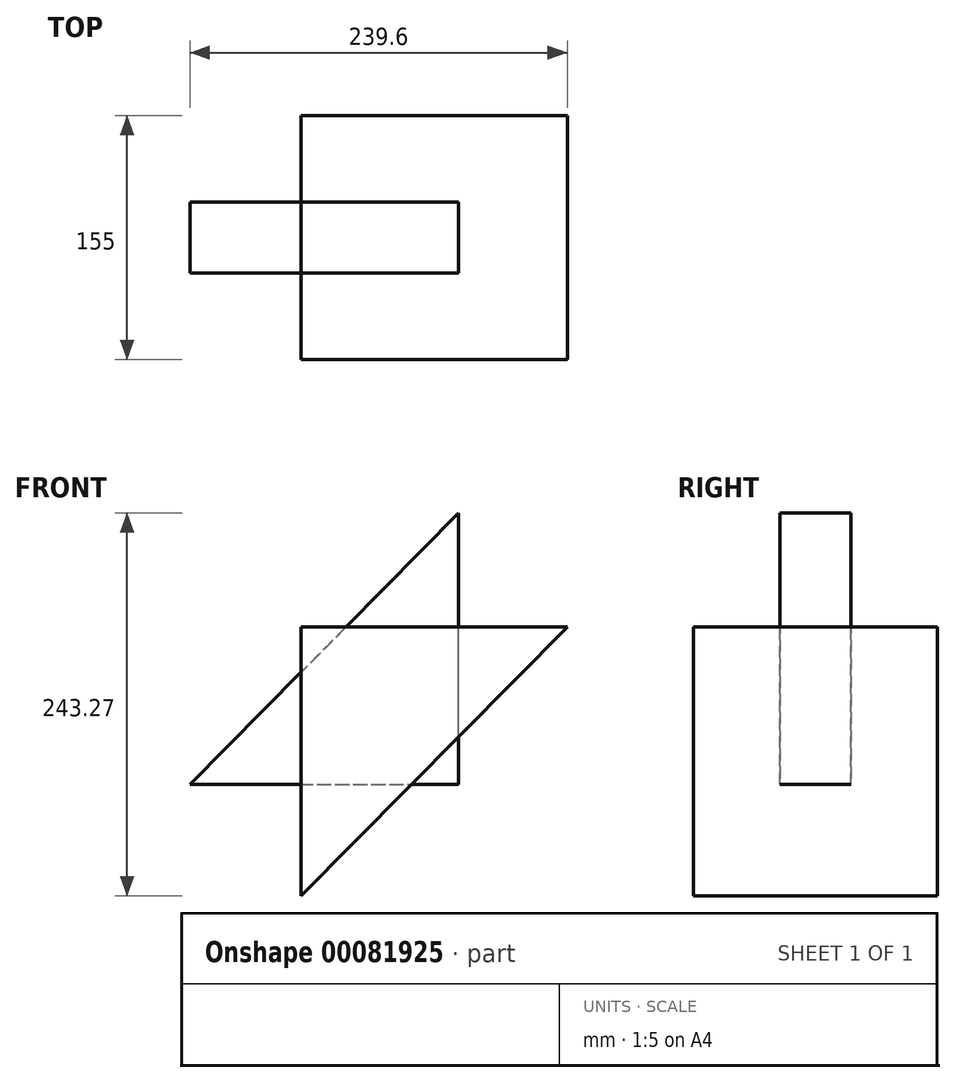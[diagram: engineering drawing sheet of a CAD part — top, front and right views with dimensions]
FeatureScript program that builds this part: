
annotation { "Feature Type Name" : "Feature", "Feature Type Description" : "" }
export const myFeature = defineFeature(function(context is Context, id is Id, definition is map)
    precondition{}
    {
        {
            var Q0;
            Q0=qCreatedBy(makeId("Front.planeOp"),FACE);
            var sketch = newSketch(context, id + "F0", { "sketchPlane" : qUnion([Q0])});
            skLineSegment(sketch, "E0.bottom", {"start": v(75, 150) * mm, "end": v(-93.98, 150) * mm});
            skLineSegment(sketch, "E0.top", {"start": v(75, -74.58) * mm, "end": v(-93.98, -74.58) * mm});
            skLineSegment(sketch, "E0.left", {"start": v(75, 150) * mm, "end": v(75, -74.58) * mm});
            skLineSegment(sketch, "E0.right", {"start": v(-93.98, 150) * mm, "end": v(-93.98, -74.58) * mm});
            skLineSegment(sketch, "E1", {"start": v(75, -74.58) * mm, "end": v(-109.95, -36.96) * mm});
            skLineSegment(sketch, "E2", {"start": v(-109.95, -36.96) * mm, "end": v(-109.95, -36.96) * mm});
            skLineSegment(sketch, "E3", {"start": v(-109.95, -36.96) * mm, "end": v(-93.98, -74.58) * mm});
            skLineSegment(sketch, "E4", {"start": v(-109.95, -36.96) * mm, "end": v(75, 150) * mm});
            skLineSegment(sketch, "E5", {"start": v(-109.95, -36.96) * mm, "end": v(-93.98, 150) * mm});
            skSolve(sketch);
        }
        {
            var Q0;
            {var subQ0=sQuery(id+"F0.wireOp",EDGE,"E0.bottom");Q0=makeQuery(id+"F0.imprint","IMPRINT",FACE,{"disambiguationData":[TD([[makeQuery(id+"F0.imprint","IMPRINT",EDGE,{"derivedFrom":subQ0}),1.0]])]});}
            extrude(context, id + "F1", {"entities" : qUnion([Q0]), "depth" : 155 * mm});
        }
        {
            var Q0;
            Q0=makeQuery(id+"F1.opExtrude","SWEPT_FACE",FACE,{"disambiguationData":[OSD([sQuery(id+"F0.wireOp",EDGE,"E4")])]});
            var Q1;
            Q1=makeQuery(id+"F1.opExtrude","CAP_FACE",FACE,{"disambiguationData":[OSD([sQuery(id+"F0.wireOp",EDGE,"E0.bottom"),sQuery(id+"F0.wireOp",EDGE,"E0.right"),sQuery(id+"F0.wireOp",EDGE,"E4")])],"isStart":false});
            var Q2;
            Q2=makeQuery(id+"F1.opExtrude","SWEPT_BODY",BODY,{"disambiguationData":[OSD([sQuery(id+"F0.wireOp",EDGE,"E0.bottom"),sQuery(id+"F0.wireOp",EDGE,"E0.right"),sQuery(id+"F0.wireOp",EDGE,"E4")])]});
            shell(context, id + "F2", {"isHollow" : true, "entities" : qUnion([Q0, Q1]), "parts" : qUnion([Q2]), "thickness" : 100 * mm});
        }
    });
